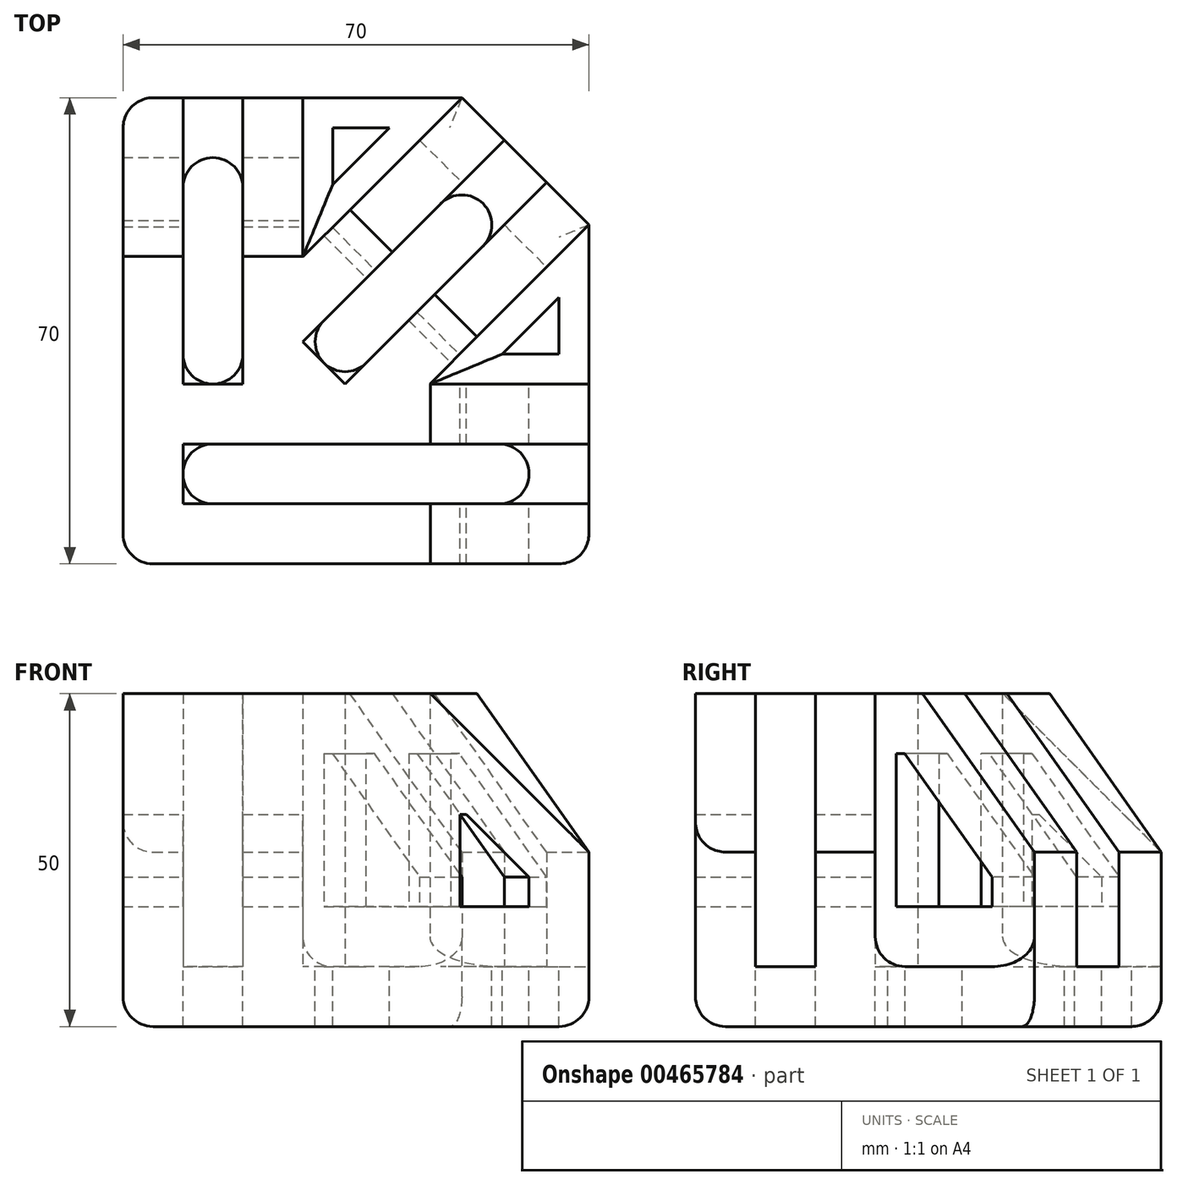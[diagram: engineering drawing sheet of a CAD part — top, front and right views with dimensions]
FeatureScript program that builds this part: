
annotation { "Feature Type Name" : "Feature", "Feature Type Description" : "" }
export const myFeature = defineFeature(function(context is Context, id is Id, definition is map)
    precondition{}
    {
        {
            var Q0;
            Q0=qCreatedBy(makeId("Top.planeOp"),FACE);
            var sketch = newSketch(context, id + "F0", { "sketchPlane" : qUnion([Q0])});
            skLineSegment(sketch, "E0", {"start": v(0, 0) * mm, "end": v(0, 70) * mm});
            skLineSegment(sketch, "E1", {"start": v(0, 70) * mm, "end": v(9, 70) * mm});
            skLineSegment(sketch, "E2", {"start": v(9, 70) * mm, "end": v(9, 27) * mm});
            skLineSegment(sketch, "E3", {"start": v(9, 27) * mm, "end": v(18, 27) * mm});
            skLineSegment(sketch, "E4", {"start": v(18, 27) * mm, "end": v(18, 70) * mm});
            skLineSegment(sketch, "E5", {"start": v(18, 70) * mm, "end": v(27, 70) * mm});
            skLineSegment(sketch, "E6", {"start": v(27, 70) * mm, "end": v(27, 46.1) * mm});
            skLineSegment(sketch, "E7", {"start": v(27, 46.1) * mm, "end": v(50.9, 70) * mm});
            skLineSegment(sketch, "E8", {"start": v(50.9, 70) * mm, "end": v(57.27, 63.64) * mm});
            skLineSegment(sketch, "E9", {"start": v(57.27, 63.64) * mm, "end": v(27, 33.36) * mm});
            skLineSegment(sketch, "E10", {"start": v(27, 33.36) * mm, "end": v(33.36, 27) * mm});
            skLineSegment(sketch, "E11", {"start": v(33.36, 27) * mm, "end": v(63.64, 57.27) * mm});
            skLineSegment(sketch, "E12", {"start": v(63.64, 57.27) * mm, "end": v(70, 50.9) * mm});
            skLineSegment(sketch, "E13", {"start": v(70, 50.9) * mm, "end": v(46.1, 27) * mm});
            skLineSegment(sketch, "E14", {"start": v(46.1, 27) * mm, "end": v(70, 27) * mm});
            skLineSegment(sketch, "E15", {"start": v(70, 27) * mm, "end": v(70, 18) * mm});
            skLineSegment(sketch, "E16", {"start": v(70, 18) * mm, "end": v(9, 18) * mm});
            skLineSegment(sketch, "E17", {"start": v(9, 18) * mm, "end": v(9, 9) * mm});
            skLineSegment(sketch, "E18", {"start": v(9, 9) * mm, "end": v(70, 9) * mm});
            skLineSegment(sketch, "E19", {"start": v(70, 9) * mm, "end": v(70, 0) * mm});
            skLineSegment(sketch, "E20", {"start": v(70, 0) * mm, "end": v(0, 0) * mm});
            skSolve(sketch);
        }
        {
            var Q0;
            Q0 = qSketchRegion(id + "F0", true);
            extrude(context, id + "F1", {"entities" : qUnion([Q0]), "depth" : 41 * mm});
        }
        {
            var Q0;
            Q0=makeQuery(id+"F1.opExtrude","CAP_FACE",FACE,{"disambiguationData":[OSD([sQuery(id+"F0.wireOp",EDGE,"E0"),sQuery(id+"F0.wireOp",EDGE,"E1"),sQuery(id+"F0.wireOp",EDGE,"E2"),sQuery(id+"F0.wireOp",EDGE,"E3"),sQuery(id+"F0.wireOp",EDGE,"E4"),sQuery(id+"F0.wireOp",EDGE,"E5"),sQuery(id+"F0.wireOp",EDGE,"E6"),sQuery(id+"F0.wireOp",EDGE,"E7"),sQuery(id+"F0.wireOp",EDGE,"E8"),sQuery(id+"F0.wireOp",EDGE,"E9"),sQuery(id+"F0.wireOp",EDGE,"E10"),sQuery(id+"F0.wireOp",EDGE,"E11"),sQuery(id+"F0.wireOp",EDGE,"E12"),sQuery(id+"F0.wireOp",EDGE,"E13"),sQuery(id+"F0.wireOp",EDGE,"E14"),sQuery(id+"F0.wireOp",EDGE,"E15"),sQuery(id+"F0.wireOp",EDGE,"E16"),sQuery(id+"F0.wireOp",EDGE,"E17"),sQuery(id+"F0.wireOp",EDGE,"E18"),sQuery(id+"F0.wireOp",EDGE,"E19"),sQuery(id+"F0.wireOp",EDGE,"E20")])],"isStart":true});
            var sketch = newSketch(context, id + "F2", { "sketchPlane" : qUnion([Q0])});
            skLineSegment(sketch, "E21", {"start": v(70, 0) * mm, "end": v(70, -50.9) * mm});
            skLineSegment(sketch, "E22", {"start": v(70, -50.9) * mm, "end": v(50.9, -70) * mm});
            skLineSegment(sketch, "E23", {"start": v(50.9, -70) * mm, "end": v(0, -70) * mm});
            skLineSegment(sketch, "E24", {"start": v(0, -70) * mm, "end": v(0, 0) * mm});
            skLineSegment(sketch, "E25", {"start": v(0, 0) * mm, "end": v(70, 0) * mm});
            skSolve(sketch);
        }
        {
            var Q0;
            Q0 = qSketchRegion(id + "F2", true);
            extrude(context, id + "F3", {"entities" : qUnion([Q0]), "operationType" : NewBodyOperationType.ADD, "depth" : 9 * mm});
        }
        {
            var Q0;
            Q0=makeQuery(id+"F1.opExtrude","CAP_EDGE",EDGE,{"disambiguationData":[OSD([sQuery(id+"F0.wireOp",EDGE,"E19")])],"isStart":false});
            var Q1;
            Q1=makeQuery(id+"F1.opExtrude","CAP_EDGE",EDGE,{"disambiguationData":[OSD([sQuery(id+"F0.wireOp",EDGE,"E15")])],"isStart":false});
            var Q2;
            Q2=makeQuery(id+"F1.opExtrude","CAP_EDGE",EDGE,{"disambiguationData":[OSD([sQuery(id+"F0.wireOp",EDGE,"E5")])],"isStart":false});
            var Q3;
            Q3=makeQuery(id+"F1.opExtrude","CAP_EDGE",EDGE,{"disambiguationData":[OSD([sQuery(id+"F0.wireOp",EDGE,"E1")])],"isStart":false});
            chamfer(context, id + "F4", {"entities" : qUnion([Q0, Q1, Q2, Q3]), "width" : 23.8 * mm, "tangentPropagation" : true});
        }
        {
            var Q0;
            Q0=makeQuery(id+"F1.opExtrude","CAP_EDGE",EDGE,{"disambiguationData":[OSD([sQuery(id+"F0.wireOp",EDGE,"E12")])],"isStart":false});
            var Q1;
            Q1=makeQuery(id+"F1.opExtrude","CAP_EDGE",EDGE,{"disambiguationData":[OSD([sQuery(id+"F0.wireOp",EDGE,"E8")])],"isStart":false});
            chamfer(context, id + "F5", {"entities" : qUnion([Q0, Q1]), "width" : 23.8 * mm, "tangentPropagation" : true});
        }
        {
            var Q0;
            {var subQ0=sQuery(id+"F2.wireOp",EDGE,"E21");Q0=makeQuery(id+"F3.boolean.opBoolean","SPLIT",FACE,{"disambiguationData":[TD([makeQuery(id+"F1.opExtrude","SWEPT_FACE",FACE,{"disambiguationData":[OSD([sQuery(id+"F0.wireOp",EDGE,"E16")])]})])],"derivedFrom":makeQuery(id+"F3.opExtrude","CAP_FACE",FACE,{"disambiguationData":[OSD([subQ0,sQuery(id+"F2.wireOp",EDGE,"E22"),sQuery(id+"F2.wireOp",EDGE,"E23"),sQuery(id+"F2.wireOp",EDGE,"E24"),sQuery(id+"F2.wireOp",EDGE,"E25")])],"isStart":true})});}
            var sketch = newSketch(context, id + "F6", { "sketchPlane" : qUnion([Q0])});
            skLineSegment(sketch, "E26.bottom", {"start": v(13.5, 27) * mm, "end": v(13.5, 27) * mm});
            skLineSegment(sketch, "E26.top", {"start": v(13.5, 61) * mm, "end": v(13.5, 61) * mm});
            skLineSegment(sketch, "E26.left", {"start": v(9, 31.5) * mm, "end": v(9, 56.5) * mm});
            skLineSegment(sketch, "E26.right", {"start": v(18, 31.5) * mm, "end": v(18, 56.5) * mm});
            skPoint(sketch, "E27.visualSharp", {"position": v(18, 61) * mm});
            skArc(sketch, "E27.filletArc", {"start": v(18, 56.5) * mm, "mid": v(16.68, 59.68) * mm, "end": v(13.5, 61) * mm});
            skPoint(sketch, "E28.visualSharp", {"position": v(9, 61) * mm});
            skArc(sketch, "E28.filletArc", {"start": v(13.5, 61) * mm, "mid": v(10.32, 59.68) * mm, "end": v(9, 56.5) * mm});
            skPoint(sketch, "E29.visualSharp", {"position": v(9, 27) * mm});
            skArc(sketch, "E29.filletArc", {"start": v(9, 31.5) * mm, "mid": v(10.32, 28.32) * mm, "end": v(13.5, 27) * mm});
            skPoint(sketch, "E30.visualSharp", {"position": v(18, 27) * mm});
            skArc(sketch, "E30.filletArc", {"start": v(13.5, 27) * mm, "mid": v(16.68, 28.32) * mm, "end": v(18, 31.5) * mm});
            skLineSegment(sketch, "E31", {"start": v(13.5, 18) * mm, "end": v(56.5, 18) * mm});
            skLineSegment(sketch, "E32", {"start": v(61, 13.5) * mm, "end": v(61, 13.5) * mm});
            skLineSegment(sketch, "E33", {"start": v(56.5, 9) * mm, "end": v(13.5, 9) * mm});
            skLineSegment(sketch, "E34", {"start": v(9, 13.5) * mm, "end": v(9, 13.5) * mm});
            skLineSegment(sketch, "E35", {"start": v(30.18, 36.55) * mm, "end": v(47.73, 54.1) * mm});
            skLineSegment(sketch, "E36", {"start": v(54.1, 54.1) * mm, "end": v(54.1, 54.1) * mm});
            skLineSegment(sketch, "E37", {"start": v(54.1, 47.73) * mm, "end": v(36.55, 30.18) * mm});
            skLineSegment(sketch, "E38", {"start": v(30.18, 30.18) * mm, "end": v(30.18, 30.18) * mm});
            skPoint(sketch, "E39.visualSharp", {"position": v(50.9, 57.27) * mm});
            skArc(sketch, "E39.filletArc", {"start": v(54.1, 54.1) * mm, "mid": v(50.9, 55.4) * mm, "end": v(47.73, 54.1) * mm});
            skPoint(sketch, "E40.visualSharp", {"position": v(57.27, 50.9) * mm});
            skArc(sketch, "E40.filletArc", {"start": v(54.1, 47.73) * mm, "mid": v(55.4, 50.9) * mm, "end": v(54.1, 54.1) * mm});
            skPoint(sketch, "E41.visualSharp", {"position": v(33.36, 27) * mm});
            skArc(sketch, "E41.filletArc", {"start": v(30.18, 30.18) * mm, "mid": v(33.36, 28.86) * mm, "end": v(36.55, 30.18) * mm});
            skPoint(sketch, "E42.visualSharp", {"position": v(27, 33.36) * mm});
            skArc(sketch, "E42.filletArc", {"start": v(30.18, 36.55) * mm, "mid": v(28.86, 33.36) * mm, "end": v(30.18, 30.18) * mm});
            skPoint(sketch, "E43.visualSharp", {"position": v(9, 18) * mm});
            skArc(sketch, "E43.filletArc", {"start": v(13.5, 18) * mm, "mid": v(10.32, 16.68) * mm, "end": v(9, 13.5) * mm});
            skPoint(sketch, "E44.visualSharp", {"position": v(9, 9) * mm});
            skArc(sketch, "E44.filletArc", {"start": v(9, 13.5) * mm, "mid": v(10.32, 10.32) * mm, "end": v(13.5, 9) * mm});
            skPoint(sketch, "E45.visualSharp", {"position": v(61, 9) * mm});
            skArc(sketch, "E45.filletArc", {"start": v(56.5, 9) * mm, "mid": v(59.68, 10.32) * mm, "end": v(61, 13.5) * mm});
            skPoint(sketch, "E46.visualSharp", {"position": v(61, 18) * mm});
            skArc(sketch, "E46.filletArc", {"start": v(61, 13.5) * mm, "mid": v(59.68, 16.68) * mm, "end": v(56.5, 18) * mm});
            skLineSegment(sketch, "E47", {"start": v(31.5, 65.5) * mm, "end": v(31.5, 56.96) * mm});
            skLineSegment(sketch, "E48", {"start": v(31.5, 56.96) * mm, "end": v(40.04, 65.5) * mm});
            skLineSegment(sketch, "E49", {"start": v(40.04, 65.5) * mm, "end": v(31.5, 65.5) * mm});
            skLineSegment(sketch, "E50", {"start": v(56.96, 31.5) * mm, "end": v(65.5, 40.04) * mm});
            skLineSegment(sketch, "E51", {"start": v(65.5, 40.04) * mm, "end": v(65.5, 31.5) * mm});
            skLineSegment(sketch, "E52", {"start": v(65.5, 31.5) * mm, "end": v(56.96, 31.5) * mm});
            skSolve(sketch);
        }
        {
            var Q0;
            Q0 = qSketchRegion(id + "F6", true);
            extrude(context, id + "F7", {"entities" : qUnion([Q0]), "operationType" : NewBodyOperationType.REMOVE, "endBound" : BoundingType.UP_TO_NEXT, "oppositeDirection" : true, "depth" : 25 * mm});
        }
        {
            var Q0;
            Q0=makeQuery(id+"F1.opExtrude","SWEPT_FACE",FACE,{"disambiguationData":[OSD([sQuery(id+"F0.wireOp",EDGE,"E13")])]});
            var sketch = newSketch(context, id + "F8", { "sketchPlane" : qUnion([Q0])});
            skLineSegment(sketch, "E53", {"start": v(56.18, 9) * mm, "end": v(76.5, 9) * mm});
            skLineSegment(sketch, "E54", {"start": v(56.18, 9) * mm, "end": v(56.18, 32) * mm});
            skLineSegment(sketch, "E55", {"start": v(76.5, 9) * mm, "end": v(76.5, 13.47) * mm});
            skLineSegment(sketch, "E56", {"start": v(76.5, 13.47) * mm, "end": v(57.97, 32) * mm});
            skLineSegment(sketch, "E57", {"start": v(57.97, 32) * mm, "end": v(56.18, 32) * mm});
            skSolve(sketch);
        }
        {
            var Q0;
            Q0 = qSketchRegion(id + "F8", true);
            extrude(context, id + "F9", {"entities" : qUnion([Q0]), "operationType" : NewBodyOperationType.REMOVE, "oppositeDirection" : true, "depth" : 28.2 * mm});
        }
        {
            var Q0;
            Q0=makeQuery(id+"F1.opExtrude","SWEPT_FACE",FACE,{"disambiguationData":[OSD([sQuery(id+"F0.wireOp",EDGE,"E6")])]});
            var sketch = newSketch(context, id + "F10", { "sketchPlane" : qUnion([Q0])});
            skLineSegment(sketch, "E58", {"start": v(50.6, 9) * mm, "end": v(61, 9) * mm});
            skLineSegment(sketch, "E59", {"start": v(61, 9) * mm, "end": v(61, 13.47) * mm});
            skLineSegment(sketch, "E60", {"start": v(61, 13.47) * mm, "end": v(51.6, 22.88) * mm});
            skLineSegment(sketch, "E61", {"start": v(51.6, 22.88) * mm, "end": v(50.6, 22.88) * mm});
            skLineSegment(sketch, "E62", {"start": v(50.6, 22.88) * mm, "end": v(50.6, 9) * mm});
            skSolve(sketch);
        }
        {
            var Q0;
            Q0 = qSketchRegion(id + "F10", true);
            extrude(context, id + "F11", {"entities" : qUnion([Q0]), "operationType" : NewBodyOperationType.REMOVE, "oppositeDirection" : true, "depth" : 34.5 * mm});
        }
        {
            var Q0;
            Q0=makeQuery(id+"F1.opExtrude","SWEPT_FACE",FACE,{"disambiguationData":[OSD([sQuery(id+"F0.wireOp",EDGE,"E14")])]});
            var sketch = newSketch(context, id + "F12", { "sketchPlane" : qUnion([Q0])});
            skLineSegment(sketch, "E63", {"start": v(-61, 9) * mm, "end": v(-61, 13.47) * mm});
            skLineSegment(sketch, "E64", {"start": v(-61, 13.47) * mm, "end": v(-51.6, 22.88) * mm});
            skLineSegment(sketch, "E65", {"start": v(-51.6, 22.88) * mm, "end": v(-50.6, 22.88) * mm});
            skLineSegment(sketch, "E66", {"start": v(-50.6, 22.88) * mm, "end": v(-50.6, 9) * mm});
            skLineSegment(sketch, "E67", {"start": v(-50.6, 9) * mm, "end": v(-61, 9) * mm});
            skSolve(sketch);
        }
        {
            var Q0;
            Q0 = qSketchRegion(id + "F12", true);
            extrude(context, id + "F13", {"entities" : qUnion([Q0]), "operationType" : NewBodyOperationType.REMOVE, "oppositeDirection" : true, "depth" : 32.2 * mm});
        }
        {
            var Q0;
            Q0=makeQuery(id+"F3.opExtrude","CAP_EDGE",EDGE,{"disambiguationData":[OSD([sQuery(id+"F2.wireOp",EDGE,"E25")])],"isStart":false});
            var Q1;
            Q1=makeQuery(id+"F3.opExtrude","CAP_EDGE",EDGE,{"disambiguationData":[OSD([sQuery(id+"F2.wireOp",EDGE,"E21")])],"isStart":false});
            var Q2;
            Q2=makeQuery(id+"F3.opExtrude","CAP_EDGE",EDGE,{"disambiguationData":[OSD([sQuery(id+"F2.wireOp",EDGE,"E22")])],"isStart":false});
            var Q3;
            Q3=makeQuery(id+"F3.opExtrude","CAP_EDGE",EDGE,{"disambiguationData":[OSD([sQuery(id+"F2.wireOp",EDGE,"E23")])],"isStart":false});
            var Q4;
            Q4=makeQuery(id+"F3.opExtrude","CAP_EDGE",EDGE,{"disambiguationData":[OSD([sQuery(id+"F2.wireOp",EDGE,"E24")])],"isStart":false});
            fillet(context, id + "F14", {"entities" : qUnion([Q0, Q1, Q2, Q3, Q4]), "radius" : 4.5 * mm, "tangentPropagation" : true, "allowEdgeOverflow" : false});
        }
        {
            var Q0;
            Q0=makeQuery(id+"F1.opExtrude","CAP_EDGE",EDGE,{"disambiguationData":[OSD([sQuery(id+"F0.wireOp",EDGE,"E13")])],"isStart":true});
            var Q1;
            Q1=makeQuery(id+"F1.opExtrude","CAP_EDGE",EDGE,{"disambiguationData":[OSD([sQuery(id+"F0.wireOp",EDGE,"E14")])],"isStart":true});
            var Q2;
            Q2=makeQuery(id+"F1.opExtrude","CAP_EDGE",EDGE,{"disambiguationData":[OSD([sQuery(id+"F0.wireOp",EDGE,"E7")])],"isStart":true});
            var Q3;
            Q3=makeQuery(id+"F1.opExtrude","CAP_EDGE",EDGE,{"disambiguationData":[OSD([sQuery(id+"F0.wireOp",EDGE,"E6")])],"isStart":true});
            var Q4;
            Q4=makeQuery(id+"F3.boolean.opBoolean","MERGE",EDGE,{"derivedFrom":[makeQuery(id+"F1.opExtrude","SWEPT_EDGE",EDGE,{"disambiguationData":[OSD([sQuery(id+"F0.wireOp",EDGE,"E0"),sQuery(id+"F0.wireOp",EDGE,"E20")])]}),makeQuery(id+"F3.opExtrude","SWEPT_EDGE",EDGE,{"disambiguationData":[OSD([sQuery(id+"F2.wireOp",EDGE,"E24"),sQuery(id+"F2.wireOp",EDGE,"E25")])]})]});
            var Q5;
            Q5=makeQuery(id+"F3.boolean.opBoolean","MERGE",EDGE,{"derivedFrom":[makeQuery(id+"F1.opExtrude","SWEPT_EDGE",EDGE,{"disambiguationData":[OSD([sQuery(id+"F0.wireOp",EDGE,"E19"),sQuery(id+"F0.wireOp",EDGE,"E20")])]}),makeQuery(id+"F3.opExtrude","SWEPT_EDGE",EDGE,{"disambiguationData":[OSD([sQuery(id+"F2.wireOp",EDGE,"E21"),sQuery(id+"F2.wireOp",EDGE,"E25")])]})]});
            var Q6;
            Q6=makeQuery(id+"F3.boolean.opBoolean","MERGE",EDGE,{"derivedFrom":[makeQuery(id+"F1.opExtrude","SWEPT_EDGE",EDGE,{"disambiguationData":[OSD([sQuery(id+"F0.wireOp",EDGE,"E0"),sQuery(id+"F0.wireOp",EDGE,"E1")])]}),makeQuery(id+"F3.opExtrude","SWEPT_EDGE",EDGE,{"disambiguationData":[OSD([sQuery(id+"F2.wireOp",EDGE,"E23"),sQuery(id+"F2.wireOp",EDGE,"E24")])]})]});
            fillet(context, id + "F15", {"entities" : qUnion([Q0, Q1, Q2, Q3, Q4, Q5, Q6]), "radius" : 4.5 * mm, "tangentPropagation" : true, "allowEdgeOverflow" : false});
        }
    });
